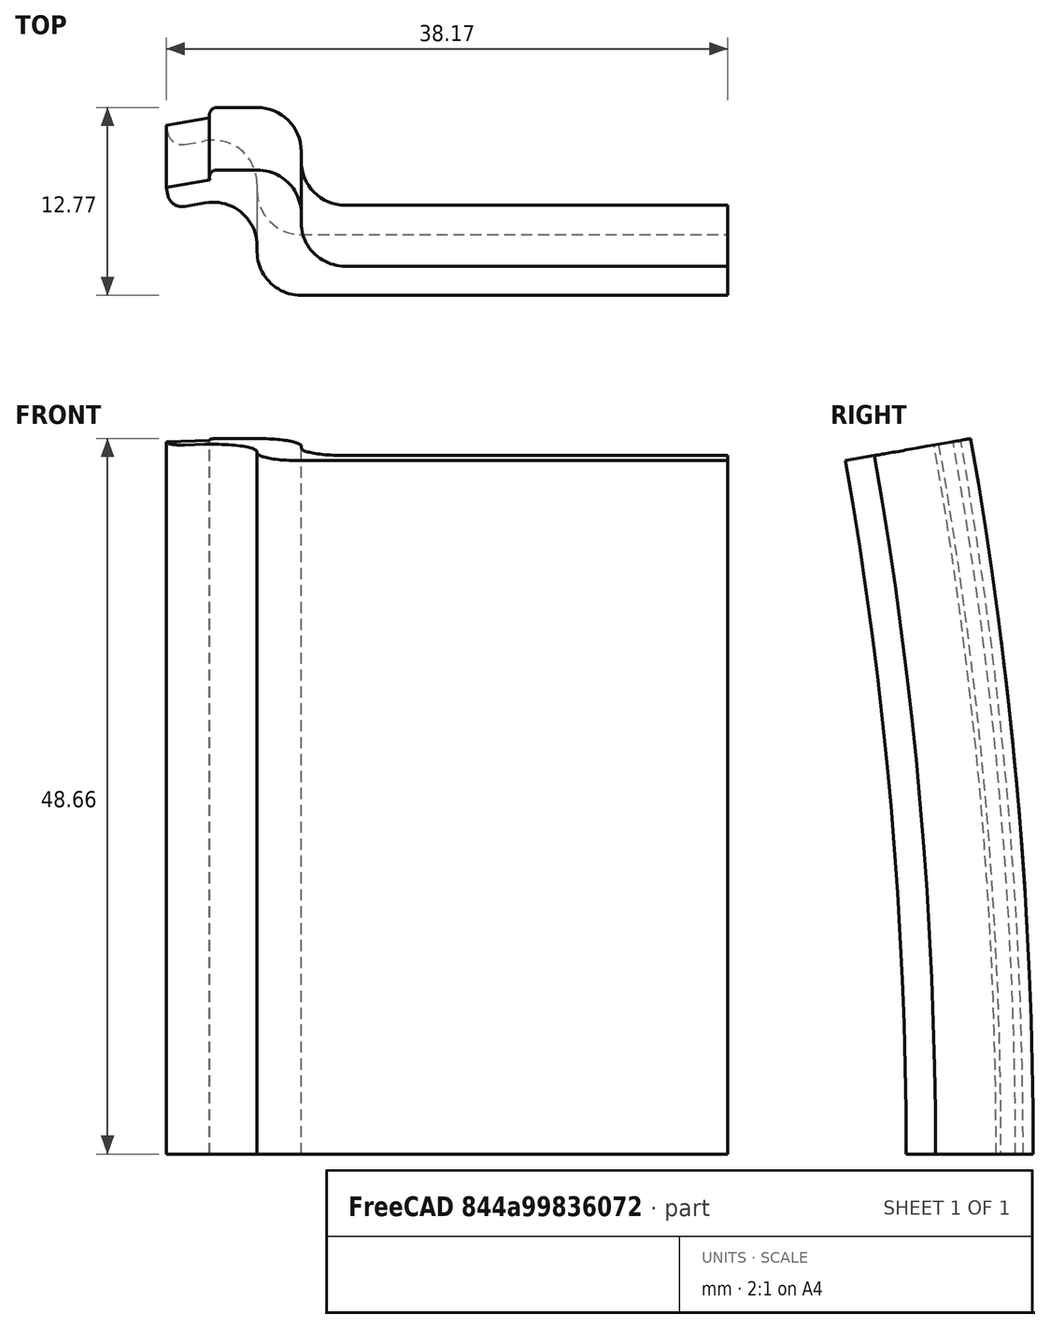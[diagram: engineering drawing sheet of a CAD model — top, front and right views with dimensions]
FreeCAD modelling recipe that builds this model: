
FCSTD DOCUMENT  (FreeCAD 0.16R)
Label: BeadLock6
License: All rights reserved
LicenseURL: http://en.wikipedia.org/wiki/All_rights_reserved
objects: PartDesign::Fillet×3, Sketcher::SketchObject×1, PartDesign::Revolution×1, Mesh::Feature×1
note: 6 computed .brp shape members not serialized (recipe doc carries the construction recipe); baked Part::Feature solids carry a one-line shape summary decoded from their .brp

FEATURE [Sketcher::SketchObject] Sketch
  sketch-geometry (10):
    g0: LineSegment StartX=0 StartY=279 StartZ=0 EndX=2.95442 EndY=279.521 EndZ=0
    g1: LineSegment StartX=2.95442 StartY=279.521 StartZ=0 EndX=2.83287 EndY=280.21 EndZ=0
    g2: LineSegment StartX=0.260472 StartY=277.523 StartZ=0 EndX=0 EndY=279 EndZ=0
    g3: LineSegment StartX=0.260472 StartY=277.523 StartZ=0 EndX=6.16932 EndY=278.565 EndZ=0
    g4: LineSegment StartX=6.16932 StartY=278.565 StartZ=0 EndX=6.16932 EndY=271.565 EndZ=0
    g5: LineSegment StartX=6.16932 StartY=271.565 StartZ=0 EndX=38.1693 EndY=271.565 EndZ=0
    g6: LineSegment StartX=38.1693 StartY=271.565 StartZ=0 EndX=38.1693 EndY=273.565 EndZ=0
    g7: LineSegment StartX=2.83287 StartY=280.21 StartZ=0 EndX=9.16932 EndY=280.21 EndZ=0
    g8: LineSegment StartX=9.16932 StartY=280.21 StartZ=0 EndX=9.16932 EndY=273.565 EndZ=0
    g9: LineSegment StartX=9.16932 StartY=273.565 StartZ=0 EndX=38.1693 EndY=273.565 EndZ=0
  constraints (30):
    c: PointOnObject(g0,g-2)
    c: DistanceY(g0) = 279
    c: Distance(g0) = 3
    c: Coincident(g1,g0)
    c: Distance(g1) = 0.7
    c: Coincident(g2,g0)
    c: Distance(g2) = 1.5
    c: Coincident(g3,g2)
    c: Distance(g3) = 6
    c: Vertical(g4)
    c: Coincident(g4,g3)
    c: Distance(g4) = 7
    c: Horizontal(g5)
    c: Coincident(g5,g4)
    c: Distance(g5) = 32
    c: Vertical(g6)
    c: Coincident(g5,g6)
    c: Distance(g6) = 2
    c: Parallel(g0,g3)
    c: Perpendicular(g0,g1)
    c: Angle(g3) = 0.174533
    c: Perpendicular(g2,g3)
    c: Coincident(g1,g7)
    c: Horizontal(g7)
    c: Coincident(g7,g8)
    c: Coincident(g8,g9)
    c: Coincident(g9,g6)
    c: Horizontal(g9)
    c: Parallel(g8,g4)
    c: Distance(g8,g4) = 3
FEATURE [PartDesign::Revolution] Revolution
  Angle = 10
  Axis = (1,0,0)
  Base = (0,0,0)
  ReferenceAxis = -> Sketch [H_Axis]
  Sketch = -> Sketch
FEATURE [PartDesign::Fillet] Fillet
  Base = -> Revolution [Edge23,Edge20,Edge11,Edge8]
  Radius = 3
FEATURE [PartDesign::Fillet] Fillet001
  Base = -> Fillet [Edge36]
  Radius = 1
FEATURE [PartDesign::Fillet] Fillet002
  Base = -> Fillet001 [Edge25]
  Radius = 0.5
FEATURE [Mesh::Feature] Mesh  label="Fillet002 (Meshed)"
